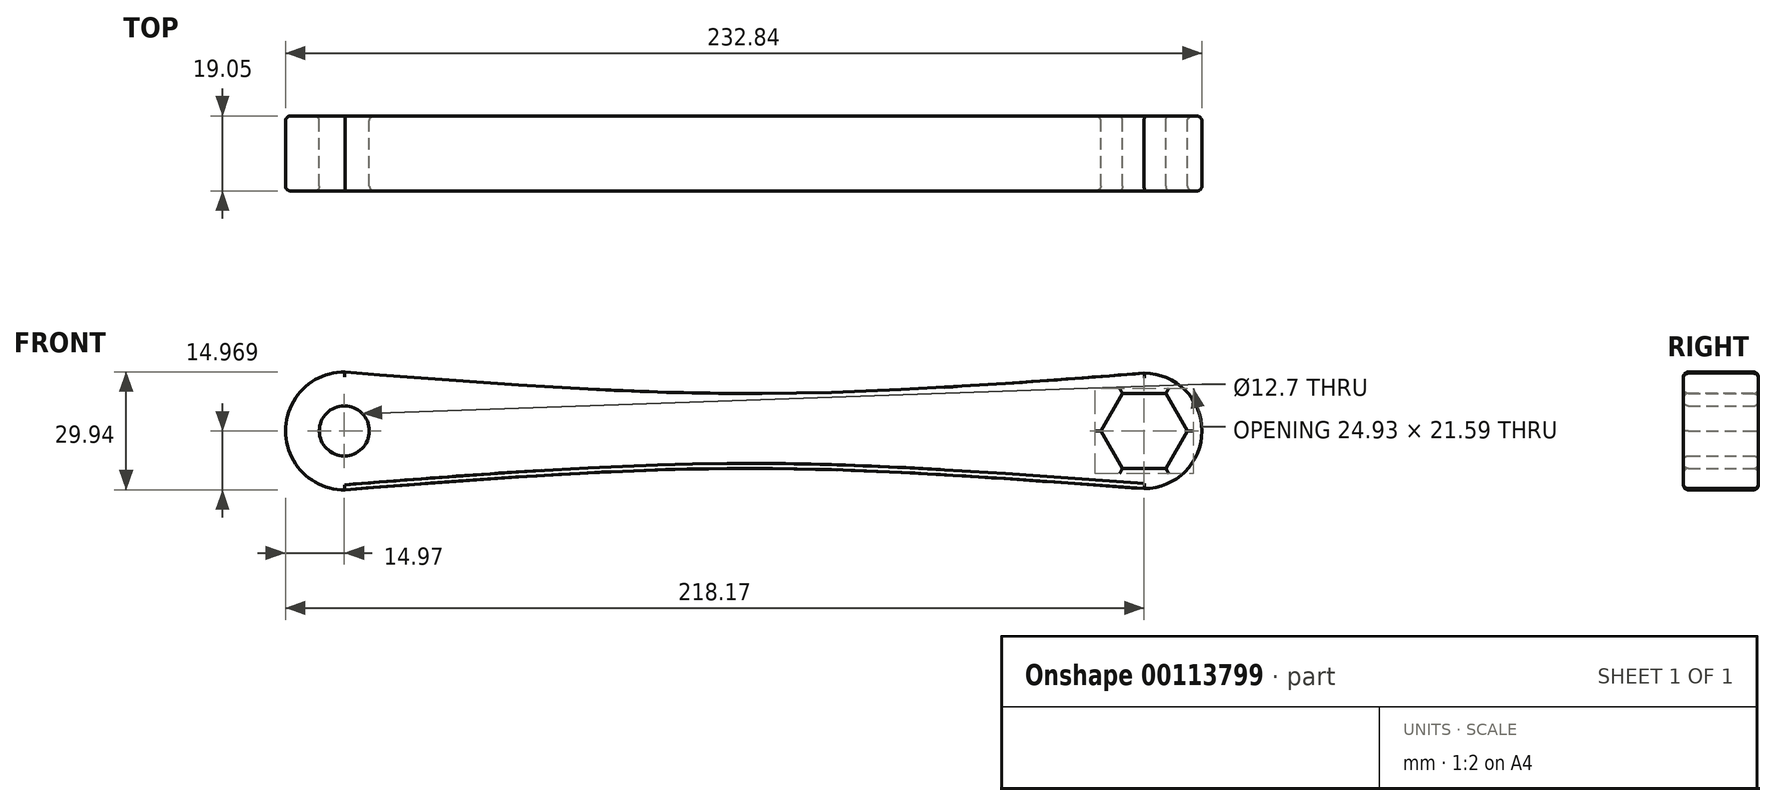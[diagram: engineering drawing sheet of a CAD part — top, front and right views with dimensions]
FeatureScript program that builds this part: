
annotation { "Feature Type Name" : "Feature", "Feature Type Description" : "" }
export const myFeature = defineFeature(function(context is Context, id is Id, definition is map)
    precondition{}
    {
        {
            var Q0;
            Q0=qCreatedBy(makeId("Front.planeOp"),FACE);
            var sketch = newSketch(context, id + "F0", { "sketchPlane" : qUnion([Q0])});
            skArc(sketch, "E0", {"start": v(-203.05, 29.64) * mm, "mid": v(-218.17, 14.67) * mm, "end": v(-203.05, -0.3) * mm});
            skArc(sketch, "E1", {"start": v(0, 29.34) * mm, "mid": v(14.67, 14.67) * mm, "end": v(0, 0) * mm});
            skCircle(sketch, "E2.cCircle", {"center": v(0, 14.67) * mm, "radius": 9.52 * mm, "construction": true});
            skLineSegment(sketch, "E2.0", {"start": v(-5.5, 24.2) * mm, "end": v(5.5, 24.2) * mm});
            skLineSegment(sketch, "E2.1", {"start": v(5.5, 24.2) * mm, "end": v(11, 14.67) * mm});
            skLineSegment(sketch, "E2.2", {"start": v(11, 14.67) * mm, "end": v(5.5, 5.14) * mm});
            skLineSegment(sketch, "E2.3", {"start": v(5.5, 5.14) * mm, "end": v(-5.5, 5.14) * mm});
            skLineSegment(sketch, "E2.4", {"start": v(-5.5, 5.14) * mm, "end": v(-11, 14.67) * mm});
            skLineSegment(sketch, "E2.5", {"start": v(-11, 14.67) * mm, "end": v(-5.5, 24.2) * mm});
            skPoint(sketch, "E2.0.midPoint", {"position": v(0, 24.2) * mm});
            skFitSpline(sketch, "E3", {"points": [v(-203.05, -0.3) * mm, v(-101.6, 5.14) * mm, v(0, 0) * mm], "startDerivative": vector(194.5, 15.59) * mm, "endDerivative": vector(211.73, -15.3) * mm});
            skFitSpline(sketch, "E4", {"points": [v(-203.05, 29.64) * mm, v(-101.6, 24.18) * mm, v(0, 29.34) * mm], "startDerivative": vector(202.93, -16.22) * mm, "endDerivative": vector(203.18, 15.62) * mm});
            skCircle(sketch, "E5", {"center": v(-203.2, 14.67) * mm, "radius": 6.35 * mm});
            skSolve(sketch);
        }
        {
            var Q0;
            Q0=makeQuery(id+"F0.imprint","IMPRINT",FACE,{"disambiguationData":[TD([[makeQuery(id+"F0.imprint","IMPRINT",EDGE,{"derivedFrom":sQuery(id+"F0.wireOp",EDGE,"E0")}),1.0]])]});
            extrude(context, id + "F1", {"entities" : qUnion([Q0]), "depth" : 19.05 * mm});
        }
        {
            var Q0;
            Q0=makeQuery(id+"F1.opExtrude","CAP_FACE",FACE,{"disambiguationData":[OSD([sQuery(id+"F0.wireOp",EDGE,"E0"),sQuery(id+"F0.wireOp",EDGE,"E1"),sQuery(id+"F0.wireOp",EDGE,"7f0c01cd-c5a7-4685-92ad-540d01ceafc4.0"),sQuery(id+"F0.wireOp",EDGE,"7f0c01cd-c5a7-4685-92ad-540d01ceafc4.1"),sQuery(id+"F0.wireOp",EDGE,"7f0c01cd-c5a7-4685-92ad-540d01ceafc4.2"),sQuery(id+"F0.wireOp",EDGE,"7f0c01cd-c5a7-4685-92ad-540d01ceafc4.3"),sQuery(id+"F0.wireOp",EDGE,"7f0c01cd-c5a7-4685-92ad-540d01ceafc4.4"),sQuery(id+"F0.wireOp",EDGE,"7f0c01cd-c5a7-4685-92ad-540d01ceafc4.5"),sQuery(id+"F0.wireOp",EDGE,"E2.0"),sQuery(id+"F0.wireOp",EDGE,"E2.1"),sQuery(id+"F0.wireOp",EDGE,"E2.2"),sQuery(id+"F0.wireOp",EDGE,"E2.3"),sQuery(id+"F0.wireOp",EDGE,"E2.4"),sQuery(id+"F0.wireOp",EDGE,"E2.5"),sQuery(id+"F0.wireOp",EDGE,"E3"),sQuery(id+"F0.wireOp",EDGE,"E4")])],"isStart":false});
            fillet(context, id + "F2", {"entities" : qUnion([Q0]), "radius" : 1.27 * mm, "tangentPropagation" : true, "allowEdgeOverflow" : false});
        }
        {
            var Q0;
            Q0=makeQuery(id+"F1.opExtrude","CAP_FACE",FACE,{"disambiguationData":[OSD([sQuery(id+"F0.wireOp",EDGE,"E0"),sQuery(id+"F0.wireOp",EDGE,"E1"),sQuery(id+"F0.wireOp",EDGE,"7f0c01cd-c5a7-4685-92ad-540d01ceafc4.0"),sQuery(id+"F0.wireOp",EDGE,"7f0c01cd-c5a7-4685-92ad-540d01ceafc4.1"),sQuery(id+"F0.wireOp",EDGE,"7f0c01cd-c5a7-4685-92ad-540d01ceafc4.2"),sQuery(id+"F0.wireOp",EDGE,"7f0c01cd-c5a7-4685-92ad-540d01ceafc4.3"),sQuery(id+"F0.wireOp",EDGE,"7f0c01cd-c5a7-4685-92ad-540d01ceafc4.4"),sQuery(id+"F0.wireOp",EDGE,"7f0c01cd-c5a7-4685-92ad-540d01ceafc4.5"),sQuery(id+"F0.wireOp",EDGE,"E2.0"),sQuery(id+"F0.wireOp",EDGE,"E2.1"),sQuery(id+"F0.wireOp",EDGE,"E2.2"),sQuery(id+"F0.wireOp",EDGE,"E2.3"),sQuery(id+"F0.wireOp",EDGE,"E2.4"),sQuery(id+"F0.wireOp",EDGE,"E2.5"),sQuery(id+"F0.wireOp",EDGE,"E3"),sQuery(id+"F0.wireOp",EDGE,"E4")])],"isStart":true});
            fillet(context, id + "F3", {"entities" : qUnion([Q0]), "radius" : 1.27 * mm, "tangentPropagation" : true, "allowEdgeOverflow" : false});
        }
    });
